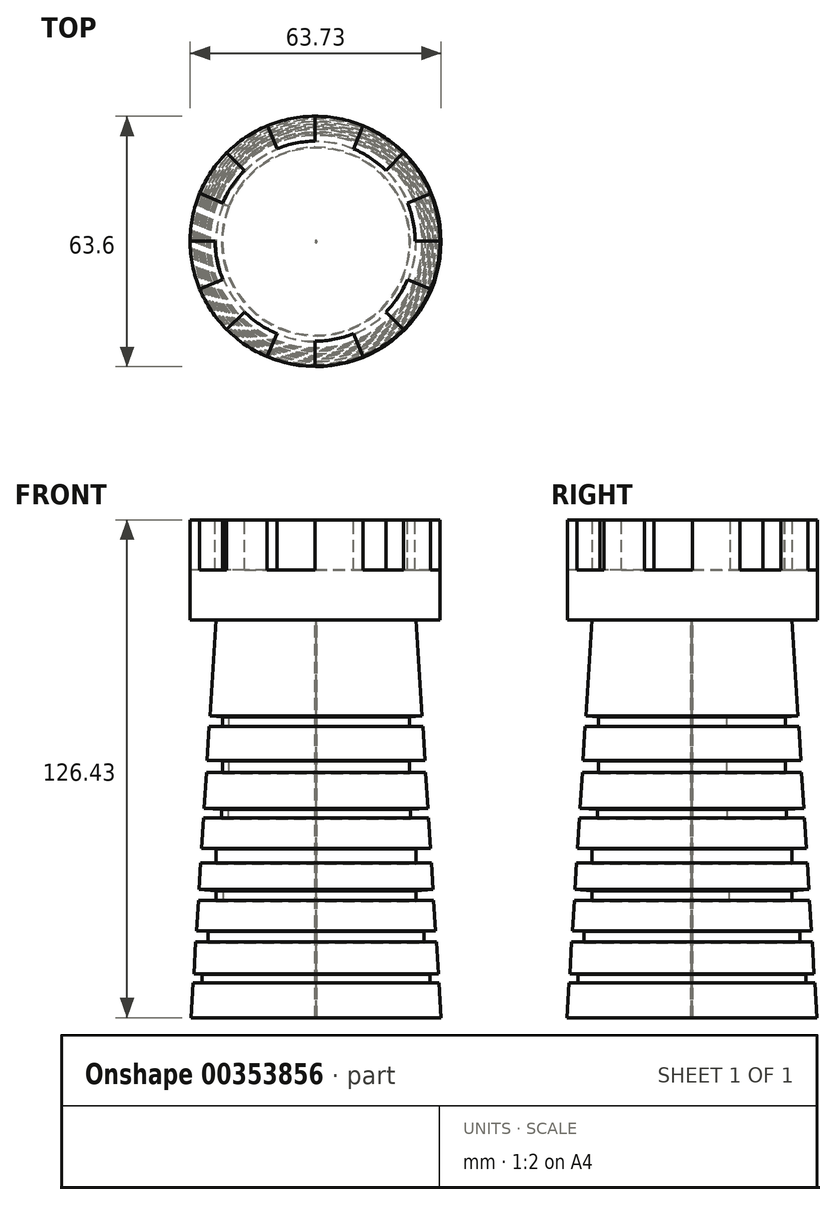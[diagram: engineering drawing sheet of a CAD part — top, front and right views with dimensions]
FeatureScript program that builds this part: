
annotation { "Feature Type Name" : "Feature", "Feature Type Description" : "" }
export const myFeature = defineFeature(function(context is Context, id is Id, definition is map)
    precondition{}
    {
        {
            var Q0;
            Q0=qCreatedBy(makeId("Top.planeOp"),FACE);
            var sketch = newSketch(context, id + "F0", { "sketchPlane" : qUnion([Q0])});
            skCircle(sketch, "E0", {"center": v(-70.03, 29.46) * mm, "radius": 31.75 * mm});
            skCircle(sketch, "E1", {"center": v(-70.03, 29.46) * mm, "radius": 25.4 * mm});
            skSolve(sketch);
        }
        {
            var Q0;
            Q0=makeQuery(id+"F0.imprint","IMPRINT",FACE,{"disambiguationData":[TD([[makeQuery(id+"F0.imprint","IMPRINT",EDGE,{"derivedFrom":sQuery(id+"F0.wireOp",EDGE,"E0")}),1.0]])]});
            var Q1;
            Q1=makeQuery(id+"F0.imprint","IMPRINT",FACE,{"disambiguationData":[TD([[makeQuery(id+"F0.imprint","IMPRINT",EDGE,{"derivedFrom":sQuery(id+"F0.wireOp",EDGE,"E1")}),1.0]])]});
            extrude(context, id + "F1", {"entities" : qUnion([Q0, Q1]), "depth" : 25.4 * mm});
        }
        {
            var Q0;
            Q0=makeQuery(id+"F1.opExtrude","CAP_FACE",FACE,{"disambiguationData":[OSD([sQuery(id+"F0.wireOp",EDGE,"E0")])],"isStart":false});
            var sketch = newSketch(context, id + "F2", { "sketchPlane" : qUnion([Q0])});
            skCircle(sketch, "E2", {"center": v(-70.03, 29.46) * mm, "radius": 25.4 * mm});
            skLineSegment(sketch, "E3", {"start": v(-95.43, 29.46) * mm, "end": v(-101.78, 29.46) * mm});
            skLineSegment(sketch, "E4", {"start": v(-44.63, 29.46) * mm, "end": v(-38.28, 29.46) * mm});
            skLineSegment(sketch, "E5", {"start": v(-70.03, 54.86) * mm, "end": v(-70.03, 61.21) * mm});
            skLineSegment(sketch, "E6", {"start": v(-70.03, 4.06) * mm, "end": v(-70.03, -2.29) * mm});
            skLineSegment(sketch, "E7", {"start": v(-52.07, 47.42) * mm, "end": v(-47.58, 51.91) * mm});
            skLineSegment(sketch, "E8", {"start": v(-87.99, 47.42) * mm, "end": v(-92.48, 51.91) * mm});
            skLineSegment(sketch, "E9", {"start": v(-87.99, 11.5) * mm, "end": v(-92.48, 7.01) * mm});
            skLineSegment(sketch, "E10", {"start": v(-52.07, 11.5) * mm, "end": v(-47.58, 7.01) * mm});
            skLineSegment(sketch, "E11", {"start": v(-99.35, 41.64) * mm, "end": v(-70.03, 29.46) * mm});
            skLineSegment(sketch, "E12", {"start": v(-70.03, 29.46) * mm, "end": v(-82.15, 58.8) * mm});
            skLineSegment(sketch, "E13", {"start": v(-70.03, 29.46) * mm, "end": v(-57.85, 58.78) * mm});
            skLineSegment(sketch, "E14", {"start": v(-70.03, 29.46) * mm, "end": v(-40.68, 41.58) * mm});
            skLineSegment(sketch, "E15", {"start": v(-70.03, 29.46) * mm, "end": v(-40.7, 17.28) * mm});
            skLineSegment(sketch, "E16", {"start": v(-70.03, 29.46) * mm, "end": v(-57.9, 0.12) * mm});
            skLineSegment(sketch, "E17", {"start": v(-70.03, 29.46) * mm, "end": v(-82.2, 0.14) * mm});
            skLineSegment(sketch, "E18", {"start": v(-70.03, 29.46) * mm, "end": v(-99.37, 17.34) * mm});
            skSolve(sketch);
        }
        {
            var Q0;
            Q0=makeQuery(id+"F2.imprint","IMPRINT",FACE,{"disambiguationData":[TD([[makeQuery(id+"F2.imprint","IMPRINT",EDGE,{"derivedFrom":sQuery(id+"F2.wireOp",EDGE,"E2")}),1.0]])]});
            var Q1;
            {var subQ0=sQuery(id+"F2.wireOp",EDGE,"E8");Q1=makeQuery(id+"F2.imprint","IMPRINT",FACE,{"disambiguationData":[TD([[makeQuery(id+"F2.imprint","IMPRINT",EDGE,{"derivedFrom":subQ0}),-1.0]])]});}
            var Q2;
            {var subQ0=sQuery(id+"F2.wireOp",EDGE,"E5");Q2=makeQuery(id+"F2.imprint","IMPRINT",FACE,{"disambiguationData":[TD([[makeQuery(id+"F2.imprint","IMPRINT",EDGE,{"derivedFrom":subQ0}),-1.0]])]});}
            var Q3;
            {var subQ0=sQuery(id+"F2.wireOp",EDGE,"E7");Q3=makeQuery(id+"F2.imprint","IMPRINT",FACE,{"disambiguationData":[TD([[makeQuery(id+"F2.imprint","IMPRINT",EDGE,{"derivedFrom":subQ0}),-1.0]])]});}
            var Q4;
            {var subQ0=sQuery(id+"F2.wireOp",EDGE,"E4");Q4=makeQuery(id+"F2.imprint","IMPRINT",FACE,{"disambiguationData":[TD([[makeQuery(id+"F2.imprint","IMPRINT",EDGE,{"derivedFrom":subQ0}),-1.0]])]});}
            var Q5;
            {var subQ0=sQuery(id+"F2.wireOp",EDGE,"E10");Q5=makeQuery(id+"F2.imprint","IMPRINT",FACE,{"disambiguationData":[TD([[makeQuery(id+"F2.imprint","IMPRINT",EDGE,{"derivedFrom":subQ0}),-1.0]])]});}
            var Q6;
            {var subQ0=sQuery(id+"F2.wireOp",EDGE,"E6");Q6=makeQuery(id+"F2.imprint","IMPRINT",FACE,{"disambiguationData":[TD([[makeQuery(id+"F2.imprint","IMPRINT",EDGE,{"derivedFrom":subQ0}),-1.0]])]});}
            var Q7;
            {var subQ0=sQuery(id+"F2.wireOp",EDGE,"E9");Q7=makeQuery(id+"F2.imprint","IMPRINT",FACE,{"disambiguationData":[TD([[makeQuery(id+"F2.imprint","IMPRINT",EDGE,{"derivedFrom":subQ0}),-1.0]])]});}
            var Q8;
            {var subQ0=sQuery(id+"F2.wireOp",EDGE,"E3");Q8=makeQuery(id+"F2.imprint","IMPRINT",FACE,{"disambiguationData":[TD([[makeQuery(id+"F2.imprint","IMPRINT",EDGE,{"derivedFrom":subQ0}),-1.0]])]});}
            extrude(context, id + "F3", {"entities" : qUnion([Q0, Q1, Q2, Q3, Q4, Q5, Q6, Q7, Q8]), "operationType" : NewBodyOperationType.REMOVE, "oppositeDirection" : true, "depth" : 12.7 * mm});
        }
        {
            var Q0;
            Q0=sQuery(id+"F2.wireOp",EDGE,"E15");
            var Q1;
            Q1=sQuery(id+"F2.wireOp",EDGE,"E11");
            extrude(context, id + "F4", {"bodyType" : ToolBodyType.SURFACE, "surfaceEntities" : qUnion([Q0, Q1]), "depth" : 25.4 * mm});
        }
        {
            var Q0;
            Q0=makeQuery(id+"F4.opExtrude","SWEPT_FACE",FACE,{"disambiguationData":[OSD([sQuery(id+"F2.wireOp",EDGE,"E11"),sQuery(id+"F2.wireOp",EDGE,"E15")])]});
            var sketch = newSketch(context, id + "F5", { "sketchPlane" : qUnion([Q0])});
            skLineSegment(sketch, "E19", {"start": v(-75.72, 0.57) * mm, "end": v(-75.72, -101.03) * mm});
            skLineSegment(sketch, "E20", {"start": v(-75.72, -101.03) * mm, "end": v(-107.47, -101.03) * mm});
            skLineSegment(sketch, "E21", {"start": v(-101.12, 0.57) * mm, "end": v(-75.72, 0.57) * mm});
            skLineSegment(sketch, "E22", {"start": v(-101.12, 0.57) * mm, "end": v(-107.47, -101.03) * mm});
            skLineSegment(sketch, "E23", {"start": v(-106.92, -92.19) * mm, "end": v(-104.62, -92.33) * mm});
            skLineSegment(sketch, "E24", {"start": v(-104.62, -92.33) * mm, "end": v(-104.62, -89.98) * mm});
            skLineSegment(sketch, "E25", {"start": v(-104.62, -89.98) * mm, "end": v(-106.77, -89.85) * mm});
            skLineSegment(sketch, "E26", {"start": v(-106.27, -81.77) * mm, "end": v(-103.15, -81.97) * mm});
            skLineSegment(sketch, "E27", {"start": v(-103.15, -81.97) * mm, "end": v(-103.15, -79.12) * mm});
            skLineSegment(sketch, "E28", {"start": v(-103.15, -79.12) * mm, "end": v(-106.1, -78.94) * mm});
            skLineSegment(sketch, "E29", {"start": v(-105.61, -71.25) * mm, "end": v(-101.1, -71.53) * mm});
            skLineSegment(sketch, "E30", {"start": v(-101.1, -71.53) * mm, "end": v(-101.1, -68.76) * mm});
            skLineSegment(sketch, "E31", {"start": v(-101.1, -68.76) * mm, "end": v(-105.44, -68.5) * mm});
            skLineSegment(sketch, "E32", {"start": v(-105.02, -61.76) * mm, "end": v(-101.13, -62) * mm});
            skLineSegment(sketch, "E33", {"start": v(-101.13, -62) * mm, "end": v(-101.13, -58.2) * mm});
            skLineSegment(sketch, "E34", {"start": v(-101.13, -58.2) * mm, "end": v(-104.78, -57.97) * mm});
            skLineSegment(sketch, "E35", {"start": v(-104.3, -50.23) * mm, "end": v(-99.68, -50.52) * mm});
            skLineSegment(sketch, "E36", {"start": v(-99.68, -50.52) * mm, "end": v(-99.68, -48.15) * mm});
            skLineSegment(sketch, "E37", {"start": v(-99.68, -48.15) * mm, "end": v(-104.15, -47.87) * mm});
            skLineSegment(sketch, "E38", {"start": v(-103.58, -38.73) * mm, "end": v(-99.48, -39) * mm});
            skLineSegment(sketch, "E39", {"start": v(-99.48, -39) * mm, "end": v(-99.48, -35.86) * mm});
            skLineSegment(sketch, "E40", {"start": v(-99.48, -35.86) * mm, "end": v(-103.58, -35.6) * mm});
            skLineSegment(sketch, "E41", {"start": v(-102.85, -27) * mm, "end": v(-99.48, -27.2) * mm});
            skLineSegment(sketch, "E42", {"start": v(-99.48, -27.2) * mm, "end": v(-99.48, -24.57) * mm});
            skLineSegment(sketch, "E43", {"start": v(-99.48, -24.57) * mm, "end": v(-102.68, -24.37) * mm});
            skSolve(sketch);
        }
        {
            var Q0;
            Q0=makeQuery(id+"F5.imprint","IMPRINT",FACE,{"disambiguationData":[TD([[makeQuery(id+"F5.imprint","IMPRINT",EDGE,{"derivedFrom":sQuery(id+"F5.wireOp",EDGE,"E19")}),-1.0]])]});
            extrude(context, id + "F6", {"entities" : qUnion([Q0]), "operationType" : NewBodyOperationType.ADD, "depth" : 0.25 * mm});
        }
        {
            var Q0;
            Q0=makeQuery(id+"F6.opExtrude","CAP_FACE",FACE,{"disambiguationData":[OSD([sQuery(id+"F5.wireOp",EDGE,"E19"),sQuery(id+"F5.wireOp",EDGE,"E20"),sQuery(id+"F5.wireOp",EDGE,"E21"),sQuery(id+"F5.wireOp",EDGE,"E22"),sQuery(id+"F5.wireOp",EDGE,"E23"),sQuery(id+"F5.wireOp",EDGE,"E24"),sQuery(id+"F5.wireOp",EDGE,"E25"),sQuery(id+"F5.wireOp",EDGE,"E26"),sQuery(id+"F5.wireOp",EDGE,"E27"),sQuery(id+"F5.wireOp",EDGE,"E28"),sQuery(id+"F5.wireOp",EDGE,"E29"),sQuery(id+"F5.wireOp",EDGE,"E30"),sQuery(id+"F5.wireOp",EDGE,"E31"),sQuery(id+"F5.wireOp",EDGE,"E32"),sQuery(id+"F5.wireOp",EDGE,"E33"),sQuery(id+"F5.wireOp",EDGE,"E34"),sQuery(id+"F5.wireOp",EDGE,"E35"),sQuery(id+"F5.wireOp",EDGE,"E36"),sQuery(id+"F5.wireOp",EDGE,"E37"),sQuery(id+"F5.wireOp",EDGE,"E38"),sQuery(id+"F5.wireOp",EDGE,"E39"),sQuery(id+"F5.wireOp",EDGE,"E40"),sQuery(id+"F5.wireOp",EDGE,"E41"),sQuery(id+"F5.wireOp",EDGE,"E42"),sQuery(id+"F5.wireOp",EDGE,"E43")])],"isStart":false});
            var Q1;
            Q1=sQuery(id+"F5.wireOp",EDGE,"E19");
            revolve(context, id + "F7", {"operationType" : NewBodyOperationType.ADD, "entities" : qUnion([Q0]), "axis" : qUnion([Q1]), "revolveType" : RevolveType.FULL});
        }
    });
